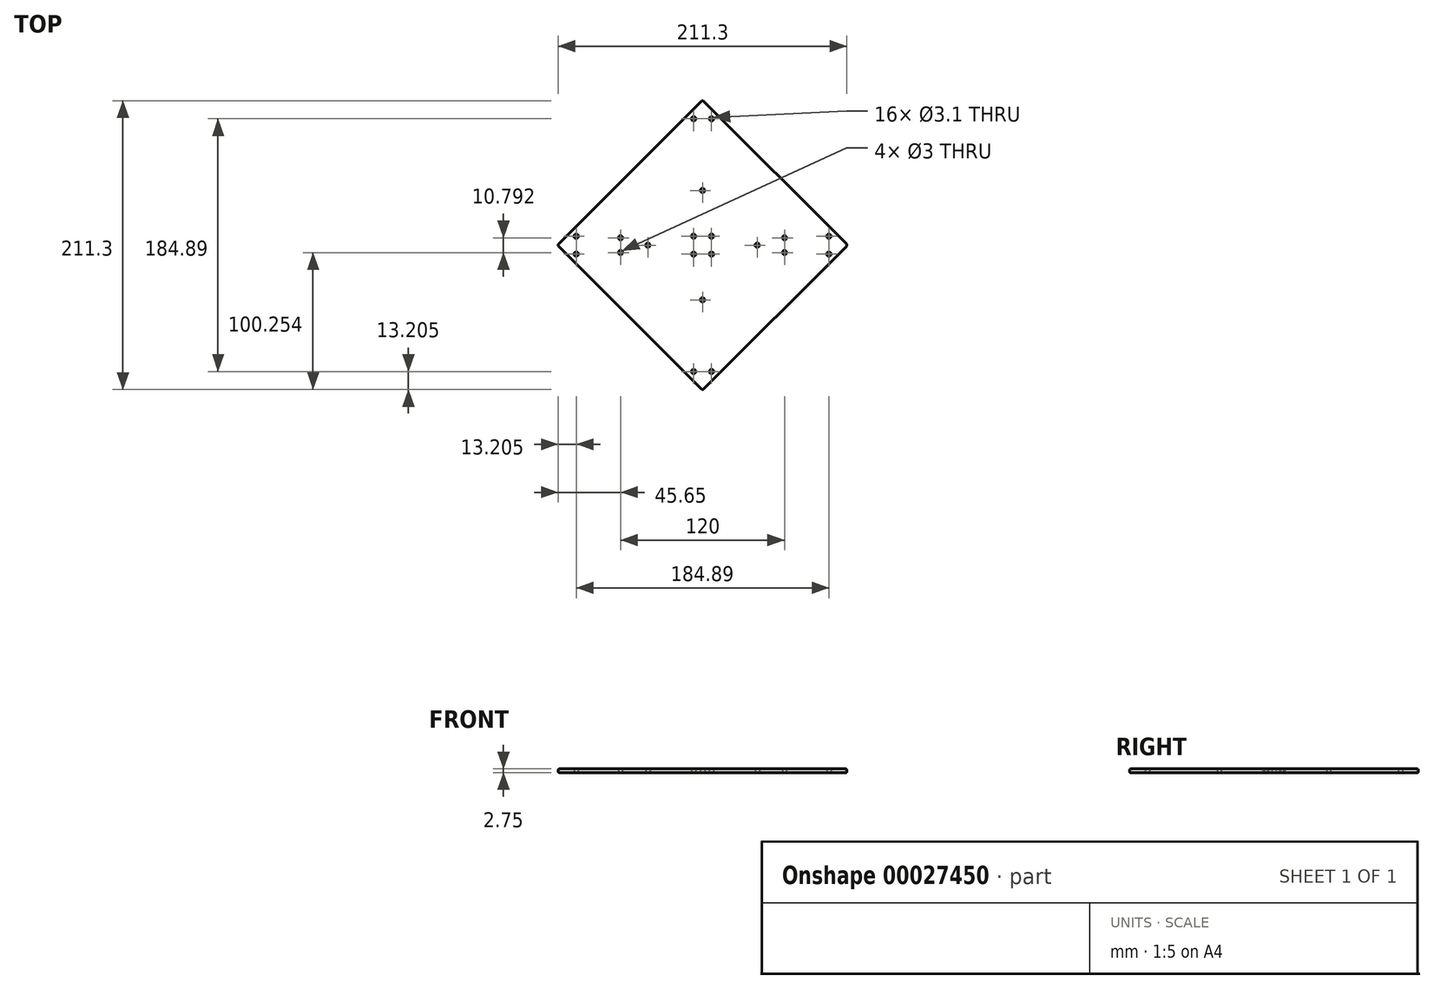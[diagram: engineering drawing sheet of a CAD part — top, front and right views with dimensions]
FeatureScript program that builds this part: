
annotation { "Feature Type Name" : "Feature", "Feature Type Description" : "" }
export const myFeature = defineFeature(function(context is Context, id is Id, definition is map)
    precondition{}
    {
        {
            var Q0;
            Q0=qCreatedBy(makeId("Top.planeOp"),FACE);
            var sketch = newSketch(context, id + "F0", { "sketchPlane" : qUnion([Q0])});
            skLineSegment(sketch, "E0", {"start": v(106.07, 0) * mm, "end": v(0, 106.07) * mm});
            skLineSegment(sketch, "E1", {"start": v(0, 106.07) * mm, "end": v(-106.07, 0) * mm});
            skLineSegment(sketch, "E2", {"start": v(-106.07, 0) * mm, "end": v(0, -106.07) * mm});
            skLineSegment(sketch, "E3", {"start": v(0, -106.07) * mm, "end": v(106.07, 0) * mm});
            skLineSegment(sketch, "E4", {"start": v(106.07, 0) * mm, "end": v(-106.07, 0) * mm, "construction": true});
            skPoint(sketch, "E5", {"position": v(0, 0) * mm});
            skCircle(sketch, "E6", {"center": v(6.55, 92.44) * mm, "radius": 1.55 * mm});
            skCircle(sketch, "E7", {"center": v(-6.55, 92.44) * mm, "radius": 1.55 * mm});
            skCircle(sketch, "E8.1.0", {"center": v(-92.44, -6.55) * mm, "radius": 1.55 * mm});
            skCircle(sketch, "E8.1.1", {"center": v(-92.44, 6.55) * mm, "radius": 1.55 * mm});
            skCircle(sketch, "E8.2.0", {"center": v(6.55, -92.44) * mm, "radius": 1.55 * mm});
            skCircle(sketch, "E8.2.1", {"center": v(-6.55, -92.44) * mm, "radius": 1.55 * mm});
            skCircle(sketch, "E8.3.0", {"center": v(92.44, 6.55) * mm, "radius": 1.55 * mm});
            skCircle(sketch, "E8.3.1", {"center": v(92.44, -6.55) * mm, "radius": 1.55 * mm});
            skCircle(sketch, "E9", {"center": v(-6.55, 6.55) * mm, "radius": 1.55 * mm});
            skCircle(sketch, "E10", {"center": v(-6.55, -6.55) * mm, "radius": 1.55 * mm});
            skLineSegment(sketch, "E11", {"start": v(0, 106.07) * mm, "end": v(0, -106.07) * mm, "construction": true});
            skCircle(sketch, "E12", {"center": v(6.55, -6.55) * mm, "radius": 1.55 * mm});
            skCircle(sketch, "E13", {"center": v(6.55, 6.55) * mm, "radius": 1.55 * mm});
            skLineSegment(sketch, "E14", {"start": v(-6.55, 6.55) * mm, "end": v(-6.55, -6.55) * mm, "construction": true});
            skLineSegment(sketch, "E15", {"start": v(6.55, -6.55) * mm, "end": v(-6.55, -6.55) * mm, "construction": true});
            skLineSegment(sketch, "E16", {"start": v(6.55, 6.55) * mm, "end": v(6.55, -6.55) * mm, "construction": true});
            skLineSegment(sketch, "E17", {"start": v(-6.55, 6.55) * mm, "end": v(6.55, 6.55) * mm, "construction": true});
            skLineSegment(sketch, "E18", {"start": v(6.55, 6.55) * mm, "end": v(-6.55, -6.55) * mm, "construction": true});
            skLineSegment(sketch, "E19", {"start": v(-53.03, 53.03) * mm, "end": v(53.03, -53.03) * mm, "construction": true});
            skLineSegment(sketch, "E20", {"start": v(53.03, 53.03) * mm, "end": v(-53.03, -53.03) * mm, "construction": true});
            skLineSegment(sketch, "E21", {"start": v(-40, 0) * mm, "end": v(0, 40) * mm, "construction": true});
            skLineSegment(sketch, "E22", {"start": v(0, 40) * mm, "end": v(40, 0) * mm, "construction": true});
            skLineSegment(sketch, "E23", {"start": v(40, 0) * mm, "end": v(0, -40) * mm, "construction": true});
            skLineSegment(sketch, "E24", {"start": v(0, -40) * mm, "end": v(-40, 0) * mm, "construction": true});
            skCircle(sketch, "E25", {"center": v(-40, 0) * mm, "radius": 1.55 * mm});
            skCircle(sketch, "E26", {"center": v(0, 40) * mm, "radius": 1.55 * mm});
            skCircle(sketch, "E27", {"center": v(40, 0) * mm, "radius": 1.55 * mm});
            skCircle(sketch, "E28", {"center": v(0, -40) * mm, "radius": 1.55 * mm});
            skCircle(sketch, "E29", {"center": v(60, -5.4) * mm, "radius": 1.5 * mm});
            skCircle(sketch, "E30", {"center": v(-60, -5.4) * mm, "radius": 1.5 * mm});
            skCircle(sketch, "E31.MirrorC", {"center": v(-60, 5.4) * mm, "radius": 1.5 * mm});
            skCircle(sketch, "E32.MirrorC", {"center": v(60, 5.4) * mm, "radius": 1.5 * mm});
            skSolve(sketch);
        }
        {
            var Q0;
            Q0 = qSketchRegion(id + "F0", true);
            extrude(context, id + "F1", {"entities" : qUnion([Q0]), "depth" : 2.75 * mm});
        }
        {
            var Q0;
            Q0=makeQuery(id+"F1.opExtrude","SWEPT_FACE",FACE,{"disambiguationData":[OSD([sQuery(id+"F0.wireOp",EDGE,"E1")])]});
            var Q1;
            Q1=makeQuery(id+"F1.opExtrude","SWEPT_FACE",FACE,{"disambiguationData":[OSD([sQuery(id+"F0.wireOp",EDGE,"E3")])]});
            var Q2;
            Q2=makeQuery(id+"F1.opExtrude","SWEPT_FACE",FACE,{"disambiguationData":[OSD([sQuery(id+"F0.wireOp",EDGE,"E2")])]});
            var Q3;
            Q3=makeQuery(id+"F1.opExtrude","SWEPT_FACE",FACE,{"disambiguationData":[OSD([sQuery(id+"F0.wireOp",EDGE,"E0")])]});
            fillet(context, id + "F2", {"entities" : qUnion([Q0, Q1, Q2, Q3]), "radius" : 1 * mm, "tangentPropagation" : true, "allowEdgeOverflow" : false});
        }
    });
